# Revit family: Hager-Vector-IP55-sistema-NoHosted-ES-es
name_source: partatom
category: Electrical Equipment
units: mm (PartAtom-declared; Revit-internal decimal feet)

## family parameters
Always vertical = Yes
Cut with Voids When Loaded = No
Panel Configuration = Two Columns, Circuits Across
Part Type = Panelboard
Room Calculation Point = No
Round Connector Dimension = Use Diameter
Shared = No
Work Plane-Based = Yes

## types (23) — shared parameters
Default Elevation = 1219 mm
EF000003 - Tipo de montaje = EV000384 - Montado superficial (escayola)
EF000007 - Color = EV000270 - Gris
EF000116 - Número RAL = 7035
EF000118 - Con placa de montaje = No
EF000339 - Tipo de cubierta = EV004216 - Puerta
EF001062 - Versión de EMC = No
EF001088 - Posibilidad de extensión = Yes
EF001134 - Carril DIN = Yes
EF001596 - Material de la carcasa = EV000139 - Plástico
EF004462 - Tipo de cierre = EV000154 - Otros
EF005474 - Grado de protección (IP) = EV006421 - IP65
EF006306 - Con cierre = No
EF009212 - Versión de la cubierta = EV000116 - Cerrado
EF015776 - Borne de tierra = No
EF015777 - Borne neutro = No
EF015941 - Puerta de transmisión de señal = Yes
HG000001 - Número de columnas = 1
HG000002 - Con puerta o tapa = Yes
HG000003 - Gama = Vector
HG000005 - Grosor = 3 mm  [stored 0.00984252 ft]
HG000006 - Empotrado = No
HG000009 - Puerta batiente doble = No
HG000010 - Puertas asimétricas = No
HG000011 - Filas vacías desde abajo = No
HG000017 - Distancia entre polos = 18 mm  [stored 0.0590551 ft]
Manufacturer = Hager
Type Comments = Vector
zero-valued in all types: EF000218 - Profundidad de instalación, EF000332 - Altura de la instalación, EF000846 - Anchura de instalación, HG000007 - Número de columnas vacías, HG000008 - Número de filas vacías

## per-type parameters (varying)
| type | EF000008 - Anchura | EF000040 - Altura | EF000049 - Profundidad | EF000266 - Número de filas | EF001131 - Profundidad interna | EF002950 - Anchura de unidades de división | EF006244 - Tapa/puerta transparente | HG000004 - Referencia del fabricante | Model |
| Montado superficial IP65 A111 A175 P93 3 unidad de división - VE103E | 111 mm | 175 mm  [stored 0.574147 ft] | 93 mm  [stored 0.305118 ft] | 1 | 93 mm  [stored 0.305118 ft] | 3 | Yes | VE103E | VE103E |
| Montado superficial IP65 A111 A175 P93 3 unidad de división - VE103F | 111 mm | 175 mm  [stored 0.574147 ft] | 93 mm  [stored 0.305118 ft] | 1 | 93 mm  [stored 0.305118 ft] | 3 | No | VE103F | VE103F |
| Montado superficial IP65 A111 A175 P93 3 unidad de división - VE103V | 111 mm | 175 mm  [stored 0.574147 ft] | 93 mm  [stored 0.305118 ft] | 1 | 93 mm  [stored 0.305118 ft] | 3 | Yes | VE103V | VE103V |
| Montado superficial IP65 A165 A190 P113 6 unidad de división - VE106E | 165 mm | 190 mm | 113 mm  [stored 0.370735 ft] | 1 | 113 mm  [stored 0.370735 ft] | 6 | Yes | VE106E | VE106E |
| Montado superficial IP65 A165 A190 P113 6 unidad de división - VE106F | 165 mm | 190 mm | 113 mm  [stored 0.370735 ft] | 1 | 113 mm  [stored 0.370735 ft] | 6 | No | VE106F | VE106F |
| Montado superficial IP65 A165 A190 P113 6 unidad de división - VE106V | 165 mm | 190 mm | 113 mm  [stored 0.370735 ft] | 1 | 113 mm  [stored 0.370735 ft] | 6 | Yes | VE106V | VE106V |
| Montado superficial IP65 A237 A210 P114 10 unidad de división - VE110E | 237 mm  [stored 0.777559 ft] | 210 mm  [stored 0.688976 ft] | 114 mm  [stored 0.374016 ft] | 1 | 114 mm  [stored 0.374016 ft] | 10 | Yes | VE110E | VE110E |
| Montado superficial IP65 A237 A210 P114 10 unidad de división - VE110F | 237 mm  [stored 0.777559 ft] | 210 mm  [stored 0.688976 ft] | 114 mm  [stored 0.374016 ft] | 1 | 114 mm  [stored 0.374016 ft] | 10 | No | VE110F | VE110F |
| Montado superficial IP65 A237 A210 P114 10 unidad de división - VE110V | 237 mm  [stored 0.777559 ft] | 210 mm  [stored 0.688976 ft] | 114 mm  [stored 0.374016 ft] | 1 | 114 mm  [stored 0.374016 ft] | 10 | Yes | VE110V | VE110V |
| Montado superficial IP65 A310 A302 P151 12 unidad de división - VE112E | 310 mm  [stored 1.01706 ft] | 302 mm  [stored 0.990814 ft] | 151 mm  [stored 0.495407 ft] | 1 | 151 mm  [stored 0.495407 ft] | 12 | Yes | VE112E | VE112E |
| Montado superficial IP65 A310 A302 P151 12 unidad de división - VE112F | 310 mm  [stored 1.01706 ft] | 302 mm  [stored 0.990814 ft] | 151 mm  [stored 0.495407 ft] | 1 | 151 mm  [stored 0.495407 ft] | 12 | No | VE112F | VE112F |
| Montado superficial IP65 A310 A427 P151 12 unidad de división - VE212E | 310 mm  [stored 1.01706 ft] | 427 mm  [stored 1.40092 ft] | 151 mm  [stored 0.495407 ft] | 2 | 151 mm  [stored 0.495407 ft] | 12 | Yes | VE212E | VE212E |
| Montado superficial IP65 A310 A427 P151 12 unidad de división - VE212F | 310 mm  [stored 1.01706 ft] | 427 mm  [stored 1.40092 ft] | 151 mm  [stored 0.495407 ft] | 2 | 151 mm  [stored 0.495407 ft] | 12 | No | VE212F | VE212F |
| Montado superficial IP65 A310 A552 P151 12 unidad de división - VE312E | 310 mm  [stored 1.01706 ft] | 552 mm  [stored 1.81102 ft] | 151 mm  [stored 0.495407 ft] | 3 | 151 mm  [stored 0.495407 ft] | 12 | Yes | VE312E | VE312E |
| Montado superficial IP65 A310 A552 P151 12 unidad de división - VE312F | 310 mm  [stored 1.01706 ft] | 552 mm  [stored 1.81102 ft] | 151 mm  [stored 0.495407 ft] | 3 | 151 mm  [stored 0.495407 ft] | 12 | No | VE312F | VE312F |
| Montado superficial IP65 A310 A677 P151 12 unidad de división - VE412E | 310 mm  [stored 1.01706 ft] | 677 mm  [stored 2.22113 ft] | 151 mm  [stored 0.495407 ft] | 4 | 151 mm  [stored 0.495407 ft] | 12 | Yes | VE412E | VE412E |
| Montado superficial IP65 A310 A677 P151 12 unidad de división - VE412F | 310 mm  [stored 1.01706 ft] | 677 mm  [stored 2.22113 ft] | 151 mm  [stored 0.495407 ft] | 4 | 151 mm  [stored 0.495407 ft] | 12 | No | VE412F | VE412F |
| Montado superficial IP65 A418 A302 P151 18 unidad de división - VE118E | 418 mm  [stored 1.37139 ft] | 302 mm  [stored 0.990814 ft] | 151 mm  [stored 0.495407 ft] | 1 | 151 mm  [stored 0.495407 ft] | 18 | Yes | VE118E | VE118E |
| Montado superficial IP65 A418 A302 P151 18 unidad de división - VE118F | 418 mm  [stored 1.37139 ft] | 302 mm  [stored 0.990814 ft] | 151 mm  [stored 0.495407 ft] | 1 | 151 mm  [stored 0.495407 ft] | 18 | No | VE118F | VE118F |
| Montado superficial IP65 A418 A452 P151 12 unidad de división - VE218E | 418 mm  [stored 1.37139 ft] | 452 mm  [stored 1.48294 ft] | 151 mm  [stored 0.495407 ft] | 2 | 151 mm  [stored 0.495407 ft] | 12 | Yes | VE218E | VE218E |
| Montado superficial IP65 A418 A452 P151 18 unidad de división - VE218F | 418 mm  [stored 1.37139 ft] | 452 mm  [stored 1.48294 ft] | 151 mm  [stored 0.495407 ft] | 2 | 151 mm  [stored 0.495407 ft] | 18 | No | VE218F | VE218F |
| Montado superficial IP65 A418 A602 P151 12 unidad de división - VE318E | 418 mm  [stored 1.37139 ft] | 602 mm  [stored 1.97507 ft] | 151 mm  [stored 0.495407 ft] | 3 | 151 mm  [stored 0.495407 ft] | 12 | Yes | VE318E | VE318E |
| Montado superficial IP65 A418 A602 P151 18 unidad de división - VE318F | 418 mm  [stored 1.37139 ft] | 602 mm  [stored 1.97507 ft] | 151 mm  [stored 0.495407 ft] | 3 | 151 mm  [stored 0.495407 ft] | 18 | No | VE318F | VE318F |

note: [stored X ft] marks values corroborated as IEEE doubles in the binary element streams (Revit-internal decimal feet)

## geometry (parser evidence)
native form markers: Sweep x13
no freeform markers — native parametric forms only
